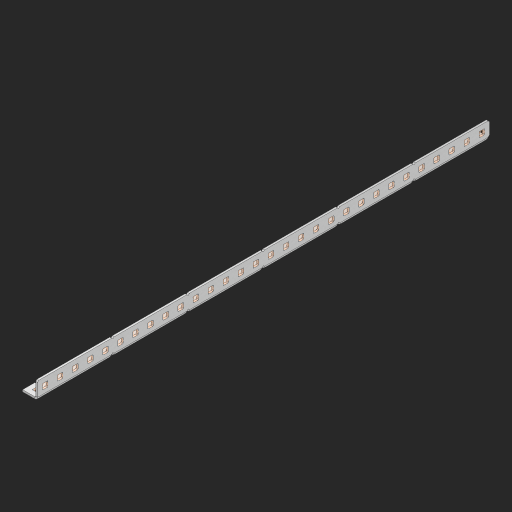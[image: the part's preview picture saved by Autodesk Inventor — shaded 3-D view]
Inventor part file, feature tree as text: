
AUTODESK INVENTOR PART (.ipt)
format: ipt  version: 2023 (Build 270158000, 158)  size: 1,261,568 bytes
history: native  units: in
note: dims shown in document units (in); Inventor stores cm internally (conversion verified against a paired STEP export)
features: other x238, extrude x88, sheet_metal_op x11, sketch x10, pattern_linear x2, mirror x1, chamfer x1
ambient origin geometry x8: Origin, YZ Plane, XZ Plane, XY Plane, X Axis, Y Axis, Z Axis, Center Point
bodies: Solid1 (feature_tree), Body (feature_tree)
feature tree (351):
  other  "Alu Half C 1x2x1x30"
  other  "Table"
  other  "Alu C 1x2x1x35"
  other  "Alu C 1x2x1x34"
  other  "Alu C 1x2x1x33"
  other  "Alu C 1x2x1x32"
  other  "Alu C 1x2x1x31"
  other  "Alu C 1x2x1x30"
  other  "Alu C 1x2x1x29"
  other  "Alu C 1x2x1x28"
  other  "Alu C 1x2x1x27"
  other  "Alu C 1x2x1x26"
  other  "Alu C 1x2x1x25"
  other  "Alu C 1x2x1x24"
  other  "Alu C 1x2x1x23"
  other  "Alu C 1x2x1x22"
  other  "Alu C 1x2x1x21"
  other  "Alu C 1x2x1x20"
  other  "Alu C 1x2x1x19"
  other  "Alu C 1x2x1x18"
  other  "Alu C 1x2x1x17"
  other  "Alu C 1x2x1x16"
  other  "Alu C 1x2x1x15"
  other  "Alu C 1x2x1x14"
  other  "Alu C 1x2x1x13"
  other  "Alu C 1x2x1x12"
  other  "Alu C 1x2x1x11"
  other  "Alu C 1x2x1x10"
  other  "Alu C 1x2x1x9"
  other  "Alu C 1x2x1x8"
  other  "Alu C 1x2x1x7"
  other  "Alu C 1x2x1x6"
  other  "Alu C 1x2x1x5"
  other  "Alu C 1x2x1x4"
  other  "Alu C 1x2x1x3"
  other  "Alu C 1x2x1x2"
  other  "Alu C 1x2x1x1"
  other  "Steel C 1x2x1x35"
  other  "Steel C 1x2x1x34"
  other  "Steel C 1x2x1x33"
  other  "Steel C 1x2x1x32"
  other  "Steel C 1x2x1x31"
  other  "Steel C 1x2x1x30"
  other  "Steel C 1x2x1x29"
  other  "Steel C 1x2x1x28"
  other  "Steel C 1x2x1x27"
  other  "Steel C 1x2x1x26"
  other  "Steel C 1x2x1x25"
  other  "Steel C 1x2x1x24"
  other  "Steel C 1x2x1x23"
  other  "Steel C 1x2x1x22"
  other  "Steel C 1x2x1x21"
  other  "Steel C 1x2x1x20"
  other  "Steel C 1x2x1x19"
  other  "Steel C 1x2x1x18"
  other  "Steel C 1x2x1x17"
  other  "Steel C 1x2x1x16"
  other  "Steel C 1x2x1x15"
  other  "Steel C 1x2x1x14"
  other  "Steel C 1x2x1x13"
  other  "Steel C 1x2x1x12"
  other  "Steel C 1x2x1x11"
  other  "Steel C 1x2x1x10"
  other  "Steel C 1x2x1x9"
  other  "Steel C 1x2x1x8"
  other  "Steel C 1x2x1x7"
  other  "Steel C 1x2x1x6"
  other  "Steel C 1x2x1x5"
  other  "Steel C 1x2x1x4"
  other  "Steel C 1x2x1x3"
  other  "Steel C 1x2x1x2"
  other  "Steel C 1x2x1x1"
  other  "Alu Half C 1x2x1x35"
  other  "Alu Half C 1x2x1x34"
  other  "Alu Half C 1x2x1x33"
  other  "Alu Half C 1x2x1x32"
  other  "Alu Half C 1x2x1x31"
  other  "Alu Half C 1x2x1x29"
  other  "Alu Half C 1x2x1x28"
  other  "Alu Half C 1x2x1x27"
  other  "Alu Half C 1x2x1x26"
  other  "Alu Half C 1x2x1x25"
  other  "Alu Half C 1x2x1x24"
  other  "Alu Half C 1x2x1x23"
  other  "Alu Half C 1x2x1x22"
  other  "Alu Half C 1x2x1x21"
  other  "Alu Half C 1x2x1x20"
  other  "Alu Half C 1x2x1x19"
  other  "Alu Half C 1x2x1x18"
  other  "Alu Half C 1x2x1x17"
  other  "Alu Half C 1x2x1x16"
  other  "Alu Half C 1x2x1x15"
  other  "Alu Half C 1x2x1x14"
  other  "Alu Half C 1x2x1x13"
  other  "Alu Half C 1x2x1x12"
  other  "Alu Half C 1x2x1x11"
  other  "Alu Half C 1x2x1x10"
  other  "Alu Half C 1x2x1x9"
  other  "Alu Half C 1x2x1x8"
  other  "Alu Half C 1x2x1x7"
  other  "Alu Half C 1x2x1x6"
  other  "Alu Half C 1x2x1x5"
  other  "Alu Half C 1x2x1x4"
  other  "Alu Half C 1x2x1x3"
  other  "Alu Half C 1x2x1x2"
  other  "Alu Half C 1x2x1x1"
  other  "Steel Half C 1x2x1x35"
  other  "Steel Half C 1x2x1x34"
  other  "Steel Half C 1x2x1x33"
  other  "Steel Half C 1x2x1x32"
  other  "Steel Half C 1x2x1x31"
  other  "Steel Half C 1x2x1x30"
  other  "Steel Half C 1x2x1x29"
  other  "Steel Half C 1x2x1x28"
  other  "Steel Half C 1x2x1x27"
  other  "Steel Half C 1x2x1x26"
  other  "Steel Half C 1x2x1x25"
  other  "Steel Half C 1x2x1x24"
  other  "Steel Half C 1x2x1x23"
  other  "Steel Half C 1x2x1x22"
  other  "Steel Half C 1x2x1x21"
  other  "Steel Half C 1x2x1x20"
  other  "Steel Half C 1x2x1x19"
  other  "Steel Half C 1x2x1x18"
  other  "Steel Half C 1x2x1x17"
  other  "Steel Half C 1x2x1x16"
  other  "Steel Half C 1x2x1x15"
  other  "Steel Half C 1x2x1x14"
  other  "Steel Half C 1x2x1x13"
  other  "Steel Half C 1x2x1x12"
  other  "Steel Half C 1x2x1x11"
  other  "Steel Half C 1x2x1x10"
  other  "Steel Half C 1x2x1x9"
  other  "Steel Half C 1x2x1x8"
  other  "Steel Half C 1x2x1x7"
  other  "Steel Half C 1x2x1x6"
  other  "Steel Half C 1x2x1x5"
  other  "Steel Half C 1x2x1x4"
  other  "Steel Half C 1x2x1x3"
  other  "Steel Half C 1x2x1x2"
  other  "Steel Half C 1x2x1x1"
  sheet_metal_op  "Flanges"
  other  "Flange Pattern Plane"
  other  "Flange Pattern Sketch"
  sheet_metal_op  "Flange Pattern"
  sheet_metal_op  "Body Pattern"
  pattern_linear  "Center Pattern"  Spacing1=0.0625in  [1 undecoded]
  other  "Arc Length"
  mirror  "Notch Mirror"
  pattern_linear  "Notch Pattern"  Spacing1=0.182in  [1 undecoded]
  chamfer  "End Chamfer"
  extrude  "Half Cut"  Depth=0.02in
  sketch  "Sketch1"  dims[d0=1.0in]
  other  "Plate1"
  sketch  "Sketch2"  dims[d1=15.0in]
  other  "Plate2"
  sheet_metal_op  "Bend1"
  sheet_metal_op  "Corner1"
  sketch  "Sketch3"  dims[d2=0.0625in]
  sketch  "Sketch7"  dims[d3=0.0625in]
  other  "Srf1"
  other  "Srf2"
  sketch  "Sketch8"  dims[d4=0.0312in]
  sketch  "Sketch9"  dims[d5=0.125in]
  other  "Srf91"
  sheet_metal_op  "Body Pattern Sketch"
  other  "Srf92"
  sketch  "Sketch13"  dims[d6=0.0625in]
  sketch  "Sketch14"  dims[d7=0.5in d8=90.0deg d9=0.0312in]
  sketch  "Sketch15"  dims[d10=0.25in]
  sketch  "Sketch16"  dims[d11=0.0625in d12=0.0625in d16=0.182in d17=0.02in d18=0.0625in d19=0.0in d20=0.25in d21=0.25in d38=11.811in d40=0.5in d41=0.3937in d43=1.0in d46=0.172in d47=1.0in d48=0.0in d49=0.182in d50=0.02in d51=0.25in d52=0.25in d53=0.0625in d54=0.0in d55=0.172in d56=1.0in d57=0.0in d58=0.25in d60=11.811in d62=0.5in d63=0.3937in d65=0.5in d85=0.1473in d86=0.1782in d88=0.04in d89=0.0625in d90=0.0in d91=0.04in d92=0.0491in d95=2.5in d96=0.04in d97=0.25in d98=45.0deg d99=0.25in d100=0.5in d101=0.0in d102=2.497in d106=0.182in d107=0.02in d108=0.5in d109=0.5in d110=0.0625in d111=0.0in d112=0.172in d113=0.5in d114=0.0in d117=0.5in d118=0.5in d119=0.5in]
  other  "Srf786"
  other  "Srf823"
  other  "Srf824"
  other  "Srf825"
  other  "Srf826"
  other  "Srf827"
  other  "Srf828"
  other  "Srf829"
  other  "Srf856"
  other  "Srf857"
  other  "Srf858"
  other  "Srf859"
  other  "Srf860"
  other  "Srf861"
  other  "Srf862"
  other  "Srf889"
  other  "Srf890"
  other  "Srf891"
  other  "Srf892"
  other  "Srf893"
  other  "Srf894"
  other  "Srf895"
  other  "Srf896"
  other  "Srf922"
  other  "Srf923"
  other  "Srf924"
  other  "Srf925"
  other  "Srf926"
  other  "Srf959"
  other  "Srf960"
  other  "Srf961"
  other  "Srf962"
  other  "Srf963"
  other  "Srf996"
  other  "Srf997"
  other  "Srf998"
  other  "Srf999"
  other  "Srf1000"
  other  "Srf1143"
  other  "Srf1144"
  other  "Srf1145"
  other  "Srf1146"
  other  "Srf1147"
  other  "Srf1148"
  other  "Srf1149"
  other  "Srf1150"
  other  "Srf1151"
  other  "Srf1152"
  other  "Srf1153"
  other  "Srf1154"
  other  "Srf1155"
  other  "Srf1156"
  other  "Srf1157"
  other  "Srf1158"
  other  "Srf1199"
  other  "Srf1200"
  other  "Srf1201"
  other  "Srf1202"
  other  "Srf1203"
  other  "Srf1204"
  other  "Srf1205"
  other  "Srf1206"
  other  "Srf1207"
  other  "Srf1208"
  other  "Srf1209"
  other  "Srf1210"
  other  "Srf1211"
  other  "Srf1212"
  other  "Srf1213"
  other  "Srf1214"
  other  "Srf1255"
  other  "Srf1256"
  other  "Srf1257"
  other  "Srf1258"
  other  "Srf1259"
  other  "Srf1260"
  other  "Srf1261"
  other  "Srf1262"
  other  "Srf1263"
  other  "Srf1264"
  other  "Srf1265"
  other  "Srf1266"
  other  "Srf1267"
  other  "Srf1268"
  other  "Srf1269"
  other  "Srf1270"
  sheet_metal_op  "Flange Stamp"
  sheet_metal_op  "Flange Circle"
  sheet_metal_op  "Body Stamp"
  sheet_metal_op  "Body Circle"
  other  "Center Stamp"
  other  "Center Circle"
  sheet_metal_op  "Notch"
  extrude  "ExtrusionSrf2"  Depth=0.0625in
  extrude  "ExtrusionSrf92"  TaperAngle=0.0deg  [1 undecoded]
  extrude  "ExtrusionSrf823"  Depth=0.25in
  extrude  "ExtrusionSrf824"  Depth=0.25in
  extrude  "ExtrusionSrf825"  Depth=0.5in
  extrude  "ExtrusionSrf826"  Depth=0.5in
  extrude  "ExtrusionSrf827"  Depth=1.0in TaperAngle=0.0deg
  extrude  "ExtrusionSrf828"  Depth=0.182in
  extrude  "ExtrusionSrf829"  Depth=0.02in
  extrude  "ExtrusionSrf856"  Depth=0.25in
  extrude  "ExtrusionSrf857"  Depth=0.25in
  extrude  "ExtrusionSrf858"  Depth=0.0625in
  extrude  "ExtrusionSrf859"  TaperAngle=0.0deg  [1 undecoded]
  extrude  "ExtrusionSrf860"  Depth=0.5in
  extrude  "ExtrusionSrf861"  Depth=1.0in TaperAngle=0.0deg
  extrude  "ExtrusionSrf862"  Depth=0.25in
  extrude  "ExtrusionSrf889"  Depth=0.5in
  extrude  "ExtrusionSrf890"  Depth=0.5in
  extrude  "ExtrusionSrf891"  Depth=0.5in
  extrude  "ExtrusionSrf892"  Depth=0.5in
  extrude  "ExtrusionSrf893"  Depth=0.5in
  extrude  "ExtrusionSrf894"  Depth=0.0625in
  extrude  "ExtrusionSrf895"  TaperAngle=0.0deg  [1 undecoded]
  extrude  "ExtrusionSrf896"  Depth=0.5in
  extrude  "ExtrusionSrf922"  Depth=0.5in
  extrude  "ExtrusionSrf923"  Depth=2.5in
  extrude  "ExtrusionSrf924"  Depth=0.25in TaperAngle=45.0deg
  extrude  "ExtrusionSrf925"  Depth=0.25in
  extrude  "ExtrusionSrf926"  Depth=0.5in TaperAngle=0.0deg
  extrude  "ExtrusionSrf959"  Depth=0.5in
  extrude  "ExtrusionSrf960"  Depth=0.182in
  extrude  "ExtrusionSrf961"  Depth=0.02in
  extrude  "ExtrusionSrf962"  Depth=0.5in
  extrude  "ExtrusionSrf963"  Depth=0.5in
  extrude  "ExtrusionSrf996"  Depth=0.0625in
  extrude  "ExtrusionSrf997"  TaperAngle=0.0deg  [1 undecoded]
  extrude  "ExtrusionSrf998"  Depth=0.5in
  extrude  "ExtrusionSrf999"  Depth=0.5in TaperAngle=0.0deg
  extrude  "ExtrusionSrf1000"  Depth=0.5in
  extrude  "ExtrusionSrf1143"  Depth=0.5in
  extrude  "ExtrusionSrf1144"  Depth=0.5in
  extrude  "ExtrusionSrf1145"  [1 undecoded]
  extrude  "ExtrusionSrf1146"  [1 undecoded]
  extrude  "ExtrusionSrf1147"  [1 undecoded]
  extrude  "ExtrusionSrf1148"  [1 undecoded]
  extrude  "ExtrusionSrf1149"  [1 undecoded]
  extrude  "ExtrusionSrf1150"  [1 undecoded]
  extrude  "ExtrusionSrf1151"  [1 undecoded]
  extrude  "ExtrusionSrf1152"  [1 undecoded]
  extrude  "ExtrusionSrf1153"  [1 undecoded]
  extrude  "ExtrusionSrf1154"  [1 undecoded]
  extrude  "ExtrusionSrf1155"  [1 undecoded]
  extrude  "ExtrusionSrf1156"  [1 undecoded]
  extrude  "ExtrusionSrf1157"  [1 undecoded]
  extrude  "ExtrusionSrf1158"  [1 undecoded]
  extrude  "ExtrusionSrf1199"  [1 undecoded]
  extrude  "ExtrusionSrf1200"  [1 undecoded]
  extrude  "ExtrusionSrf1201"  [1 undecoded]
  extrude  "ExtrusionSrf1202"  [1 undecoded]
  extrude  "ExtrusionSrf1203"  [1 undecoded]
  extrude  "ExtrusionSrf1204"  [1 undecoded]
  extrude  "ExtrusionSrf1205"  [1 undecoded]
  extrude  "ExtrusionSrf1206"  [1 undecoded]
  extrude  "ExtrusionSrf1207"  [1 undecoded]
  extrude  "ExtrusionSrf1208"  [1 undecoded]
  extrude  "ExtrusionSrf1209"  [1 undecoded]
  extrude  "ExtrusionSrf1210"  [1 undecoded]
  extrude  "ExtrusionSrf1211"  [1 undecoded]
  extrude  "ExtrusionSrf1212"  [1 undecoded]
  extrude  "ExtrusionSrf1213"  [1 undecoded]
  extrude  "ExtrusionSrf1214"  [1 undecoded]
  extrude  "ExtrusionSrf1255"  [1 undecoded]
  extrude  "ExtrusionSrf1256"  [1 undecoded]
  extrude  "ExtrusionSrf1257"  [1 undecoded]
  extrude  "ExtrusionSrf1258"  [1 undecoded]
  extrude  "ExtrusionSrf1259"  [1 undecoded]
  extrude  "ExtrusionSrf1260"  [1 undecoded]
  extrude  "ExtrusionSrf1261"  [1 undecoded]
  extrude  "ExtrusionSrf1262"  [1 undecoded]
  extrude  "ExtrusionSrf1263"  [1 undecoded]
  extrude  "ExtrusionSrf1264"  [1 undecoded]
  extrude  "ExtrusionSrf1265"  [1 undecoded]
  extrude  "ExtrusionSrf1266"  [1 undecoded]
  extrude  "ExtrusionSrf1267"  [1 undecoded]
  extrude  "ExtrusionSrf1268"  [1 undecoded]
  extrude  "ExtrusionSrf1269"  [1 undecoded]
  extrude  "ExtrusionSrf1270"  [1 undecoded]
note: 52 required parameter values undecoded (feature->parameter linkage not recoverable at this tier; creation-order binding heuristic only, values carry confidence <= 0.55)
